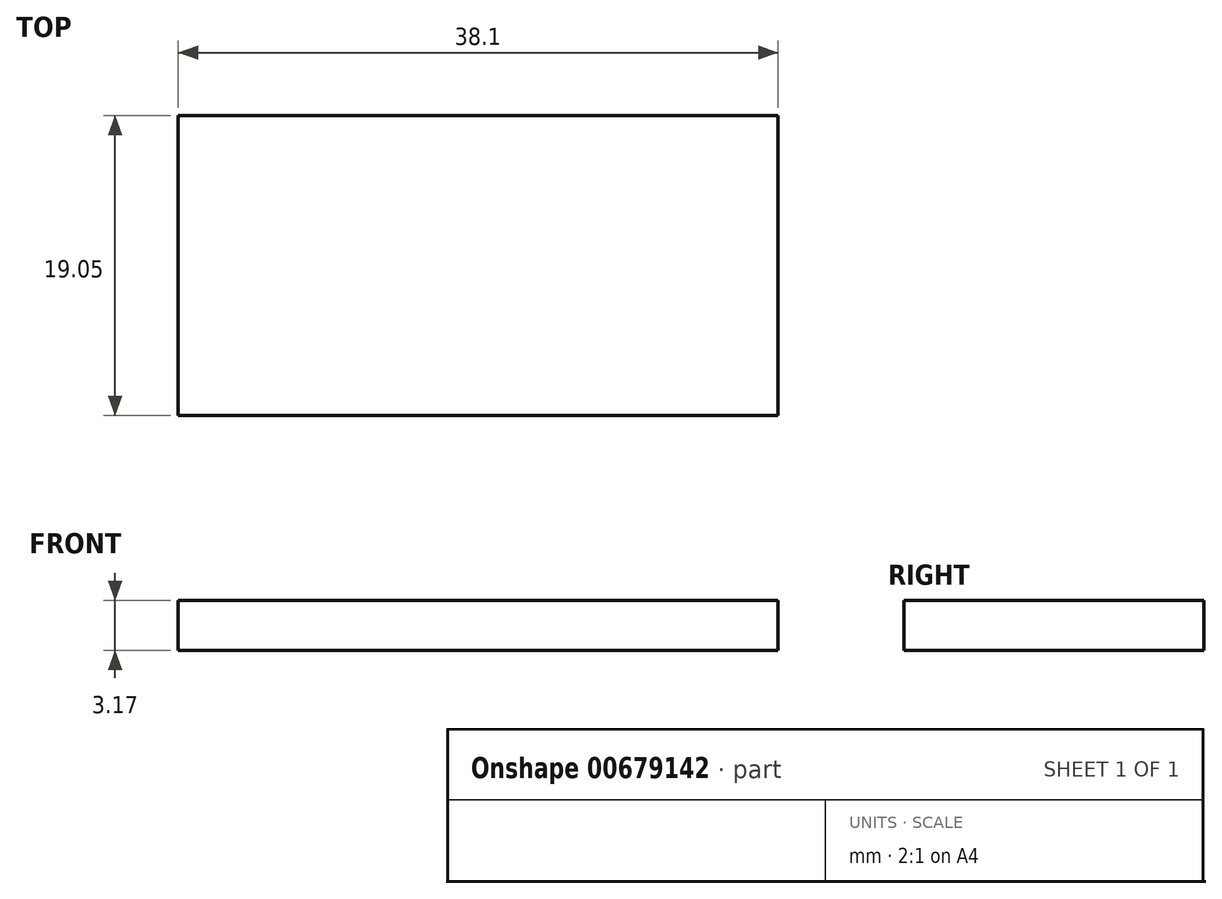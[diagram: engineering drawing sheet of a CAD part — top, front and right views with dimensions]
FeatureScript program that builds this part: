
annotation { "Feature Type Name" : "Feature", "Feature Type Description" : "" }
export const myFeature = defineFeature(function(context is Context, id is Id, definition is map)
    precondition{}
    {
        {
            var Q0;
            Q0=qCreatedBy(makeId("Top.planeOp"),FACE);
            var sketch = newSketch(context, id + "F0", { "sketchPlane" : qUnion([Q0])});
            skLineSegment(sketch, "E0.bottom", {"start": v(0, 2.12) * mm, "end": v(-38.1, 2.12) * mm});
            skLineSegment(sketch, "E0.top", {"start": v(0, 21.17) * mm, "end": v(-38.1, 21.17) * mm});
            skLineSegment(sketch, "E0.left", {"start": v(0, 2.12) * mm, "end": v(0, 21.17) * mm});
            skLineSegment(sketch, "E0.right", {"start": v(-38.1, 2.12) * mm, "end": v(-38.1, 21.17) * mm});
            skSolve(sketch);
        }
        {
            var Q0;
            Q0 = qSketchRegion(id + "F0", true);
            extrude(context, id + "F1", {"entities" : qUnion([Q0]), "depth" : 3.17 * mm, "offsetDistance" : 25.4 * mm});
        }
    });
